# Revit family: Seat_Elongated-American_Standard-Laurel-5311_Series
name_source: partatom
category: Specialty Equipment
revit_build: Autodesk Revit 2014 (Build: 20130308_1515(x64)
units: mm (PartAtom-declared; Revit-internal decimal feet)

## types (3) — shared parameters
Assembly Code = D2010110
Bowl Shape = Elongated
Default Elevation = 0"
Description = Laurel Toilet Seat
Height = 1 1/2"
Installation Type = Surface Mounted
Length = 18 1/2"
Manufacturer = American Standard
Price = Prices may vary. Please consult Manufacturer Representative for most up-to-date price list.
Product Documentation Link = https://www.americanstandard-us.com
Product Page URL = https://www.americanstandard-us.com
URL = https://www.americanstandard-us.com
Width = 14 1/4"

## per-type parameters (varying)
| type | Finish | Material |
| 5311.012.020 | Polypropylene-American Standard-020-White | Polypropylene-American Standard-020-White |
| 5311.012.021 | Polypropylene-American Standard-021-Bone | Polypropylene-American Standard-021-Bone |
| 5311.012.222 | Polypropylene-American Standard-222-Linen | Polypropylene-American Standard-222-Linen |

note: column(s) folded — value = type name in every type: Model

## geometry (parser evidence)
native form markers: Sweep x1
no freeform markers — native parametric forms only
